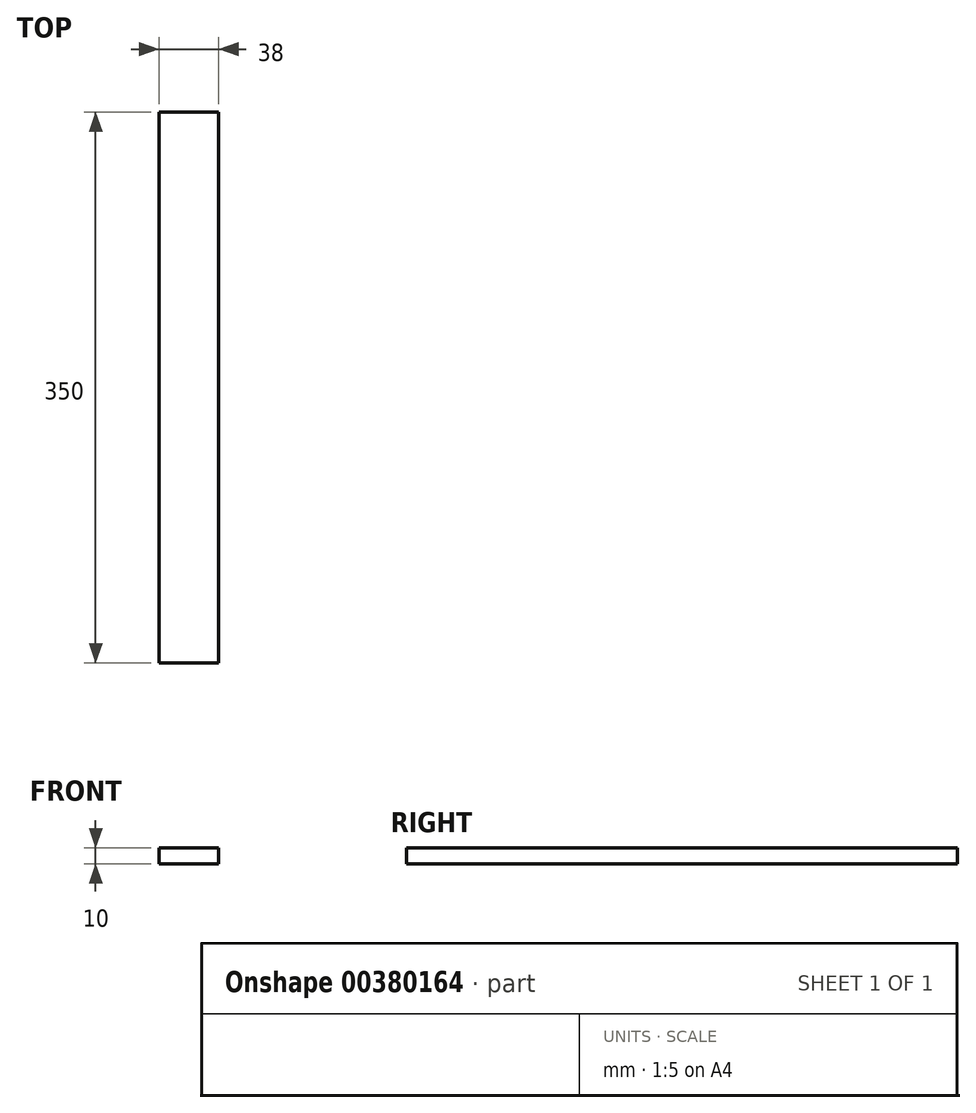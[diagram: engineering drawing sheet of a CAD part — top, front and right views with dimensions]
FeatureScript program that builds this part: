
annotation { "Feature Type Name" : "Feature", "Feature Type Description" : "" }
export const myFeature = defineFeature(function(context is Context, id is Id, definition is map)
    precondition{}
    {
        {
            var Q0;
            Q0=qCreatedBy(makeId("Front.planeOp"),FACE);
            var sketch = newSketch(context, id + "F0", { "sketchPlane" : qUnion([Q0])});
            skLineSegment(sketch, "E0.bottom", {"start": v(19, -5) * mm, "end": v(-19, -5) * mm});
            skLineSegment(sketch, "E0.top", {"start": v(19, 5) * mm, "end": v(-19, 5) * mm});
            skLineSegment(sketch, "E0.left", {"start": v(19, -5) * mm, "end": v(19, 5) * mm});
            skLineSegment(sketch, "E0.right", {"start": v(-19, -5) * mm, "end": v(-19, 5) * mm});
            skPoint(sketch, "E0.middle", {"position": v(0, 0) * mm});
            skSolve(sketch);
        }
        {
            var Q0;
            Q0 = qSketchRegion(id + "F0", true);
            extrude(context, id + "F1", {"entities" : qUnion([Q0]), "depth" : 350 * mm});
        }
    });
